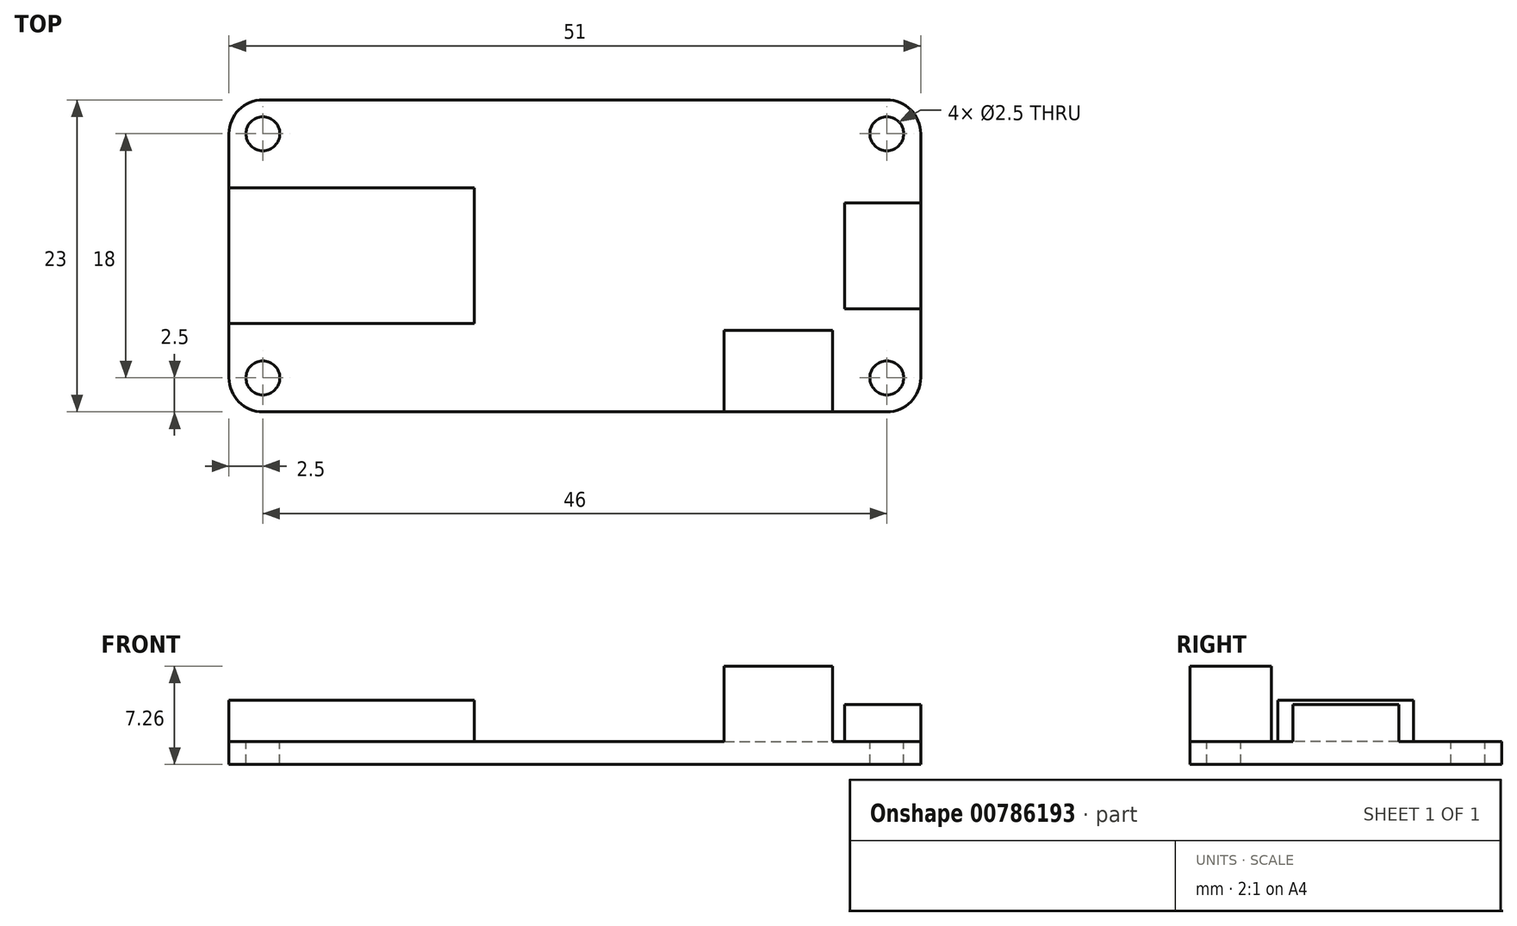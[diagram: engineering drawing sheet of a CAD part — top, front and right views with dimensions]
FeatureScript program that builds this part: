
annotation { "Feature Type Name" : "Feature", "Feature Type Description" : "" }
export const myFeature = defineFeature(function(context is Context, id is Id, definition is map)
    precondition{}
    {
        {
            assignVariable(context, id + "F0", {"name" : "board_thickness", "anyValue" : 1.7 * mm});
        }
        {
            assignVariable(context, id + "F1", {"name" : "jst_height", "anyValue" : 5.56});
        }
        {
            assignVariable(context, id + "F2", {"name" : "usb_height", "anyValue" : 2.7 * mm});
        }
        {
            assignVariable(context, id + "F3", {"name" : "ble_height", "anyValue" : 3.05 * mm});
        }
        {
            var Q0;
            Q0=qCreatedBy(makeId("Top.planeOp"),FACE);
            var sketch = newSketch(context, id + "F4", { "sketchPlane" : qUnion([Q0])});
            skLineSegment(sketch, "E0.bottom", {"start": v(-23, 11.5) * mm, "end": v(23, 11.5) * mm});
            skLineSegment(sketch, "E0.top", {"start": v(-23, -11.5) * mm, "end": v(23, -11.5) * mm});
            skLineSegment(sketch, "E0.left", {"start": v(-25.5, 9) * mm, "end": v(-25.5, -9) * mm});
            skLineSegment(sketch, "E0.right", {"start": v(25.5, 9) * mm, "end": v(25.5, -9) * mm});
            skPoint(sketch, "E1", {"position": v(0, 0) * mm});
            skCircle(sketch, "E2", {"center": v(-23, 9) * mm, "radius": 1.25 * mm});
            skLineSegment(sketch, "E3", {"start": v(-25.5, 11.5) * mm, "end": v(25.5, -11.5) * mm, "construction": true});
            skCircle(sketch, "E4.MirrorC", {"center": v(23, 9) * mm, "radius": 1.25 * mm});
            skCircle(sketch, "E5.MirrorC", {"center": v(-23, -9) * mm, "radius": 1.25 * mm});
            skCircle(sketch, "E6.MirrorC", {"center": v(23, -9) * mm, "radius": 1.25 * mm});
            skPoint(sketch, "E7.visualSharp", {"position": v(-25.5, 11.5) * mm});
            skArc(sketch, "E7.filletArc", {"start": v(-23, 11.5) * mm, "mid": v(-24.77, 10.77) * mm, "end": v(-25.5, 9) * mm});
            skPoint(sketch, "E8.visualSharp", {"position": v(-25.5, -11.5) * mm});
            skArc(sketch, "E8.filletArc", {"start": v(-25.5, -9) * mm, "mid": v(-24.77, -10.77) * mm, "end": v(-23, -11.5) * mm});
            skPoint(sketch, "E9.visualSharp", {"position": v(25.5, -11.5) * mm});
            skArc(sketch, "E9.filletArc", {"start": v(23, -11.5) * mm, "mid": v(24.77, -10.77) * mm, "end": v(25.5, -9) * mm});
            skPoint(sketch, "E10.visualSharp", {"position": v(25.5, 11.5) * mm});
            skArc(sketch, "E10.filletArc", {"start": v(25.5, 9) * mm, "mid": v(24.77, 10.77) * mm, "end": v(23, 11.5) * mm});
            skLineSegment(sketch, "E11.bottom", {"start": v(11, -5.5) * mm, "end": v(19, -5.5) * mm});
            skLineSegment(sketch, "E11.top", {"start": v(11, -11.5) * mm, "end": v(19, -11.5) * mm});
            skLineSegment(sketch, "E11.left", {"start": v(11, -5.5) * mm, "end": v(11, -11.5) * mm});
            skLineSegment(sketch, "E11.right", {"start": v(19, -5.5) * mm, "end": v(19, -11.5) * mm});
            skLineSegment(sketch, "E12.bottom", {"start": v(19.9, 3.9) * mm, "end": v(25.5, 3.9) * mm});
            skLineSegment(sketch, "E12.top", {"start": v(19.9, -3.9) * mm, "end": v(25.5, -3.9) * mm});
            skLineSegment(sketch, "E12.left", {"start": v(19.9, 3.9) * mm, "end": v(19.9, -3.9) * mm});
            skLineSegment(sketch, "E12.right", {"start": v(25.5, 3.9) * mm, "end": v(25.5, -3.9) * mm});
            skPoint(sketch, "E13", {"position": v(19.9, 0) * mm});
            skLineSegment(sketch, "E14.bottom", {"start": v(-25.5, 5) * mm, "end": v(-7.4, 5) * mm});
            skLineSegment(sketch, "E14.top", {"start": v(-25.5, -5) * mm, "end": v(-7.4, -5) * mm});
            skLineSegment(sketch, "E14.left", {"start": v(-25.5, 5) * mm, "end": v(-25.5, -5) * mm});
            skLineSegment(sketch, "E14.right", {"start": v(-7.4, 5) * mm, "end": v(-7.4, -5) * mm});
            skPoint(sketch, "E15", {"position": v(-7.4, 0) * mm});
            skSolve(sketch);
        }
        {
            var Q0;
            Q0=makeQuery(id+"F4.imprint","IMPRINT",FACE,{"disambiguationData":[TD([[makeQuery(id+"F4.imprint","IMPRINT",EDGE,{"derivedFrom":sQuery(id+"F4.wireOp",EDGE,"E0.bottom")}),-1.0]])]});
            var Q1;
            Q1=makeQuery(id+"F4.imprint","IMPRINT",FACE,{"disambiguationData":[TD([[makeQuery(id+"F4.imprint","IMPRINT",EDGE,{"derivedFrom":sQuery(id+"F4.wireOp",EDGE,"E14.bottom")}),-1.0]])]});
            var Q2;
            Q2=makeQuery(id+"F4.imprint","IMPRINT",FACE,{"disambiguationData":[TD([[makeQuery(id+"F4.imprint","IMPRINT",EDGE,{"derivedFrom":sQuery(id+"F4.wireOp",EDGE,"E11.bottom")}),-1.0]])]});
            var Q3;
            Q3=makeQuery(id+"F4.imprint","IMPRINT",FACE,{"disambiguationData":[TD([[makeQuery(id+"F4.imprint","IMPRINT",EDGE,{"derivedFrom":sQuery(id+"F4.wireOp",EDGE,"E12.bottom")}),-1.0]])]});
            extrude(context, id + "F5", {"entities" : qUnion([Q0, Q1, Q2, Q3]), "oppositeDirection" : true, "depth" : getVariable(context, 'board_thickness'), "offsetDistance" : 25 * mm});
        }
        {
            var Q0;
            Q0=makeQuery(id+"F4.imprint","IMPRINT",FACE,{"disambiguationData":[TD([[makeQuery(id+"F4.imprint","IMPRINT",EDGE,{"derivedFrom":sQuery(id+"F4.wireOp",EDGE,"E11.bottom")}),-1.0]])]});
            extrude(context, id + "F6", {"entities" : qUnion([Q0]), "operationType" : NewBodyOperationType.ADD, "depth" : (getVariable(context, 'jst_height')) * mm, "offsetDistance" : 25 * mm});
        }
        {
            var Q0;
            Q0=makeQuery(id+"F4.imprint","IMPRINT",FACE,{"disambiguationData":[TD([[makeQuery(id+"F4.imprint","IMPRINT",EDGE,{"derivedFrom":sQuery(id+"F4.wireOp",EDGE,"E14.bottom")}),-1.0]])]});
            extrude(context, id + "F7", {"entities" : qUnion([Q0]), "operationType" : NewBodyOperationType.ADD, "depth" : getVariable(context, 'ble_height'), "offsetDistance" : 25 * mm});
        }
        {
            var Q0;
            Q0=makeQuery(id+"F4.imprint","IMPRINT",FACE,{"disambiguationData":[TD([[makeQuery(id+"F4.imprint","IMPRINT",EDGE,{"derivedFrom":sQuery(id+"F4.wireOp",EDGE,"E12.bottom")}),-1.0]])]});
            extrude(context, id + "F8", {"entities" : qUnion([Q0]), "operationType" : NewBodyOperationType.ADD, "depth" : getVariable(context, 'usb_height'), "offsetDistance" : 25 * mm});
        }
    });
